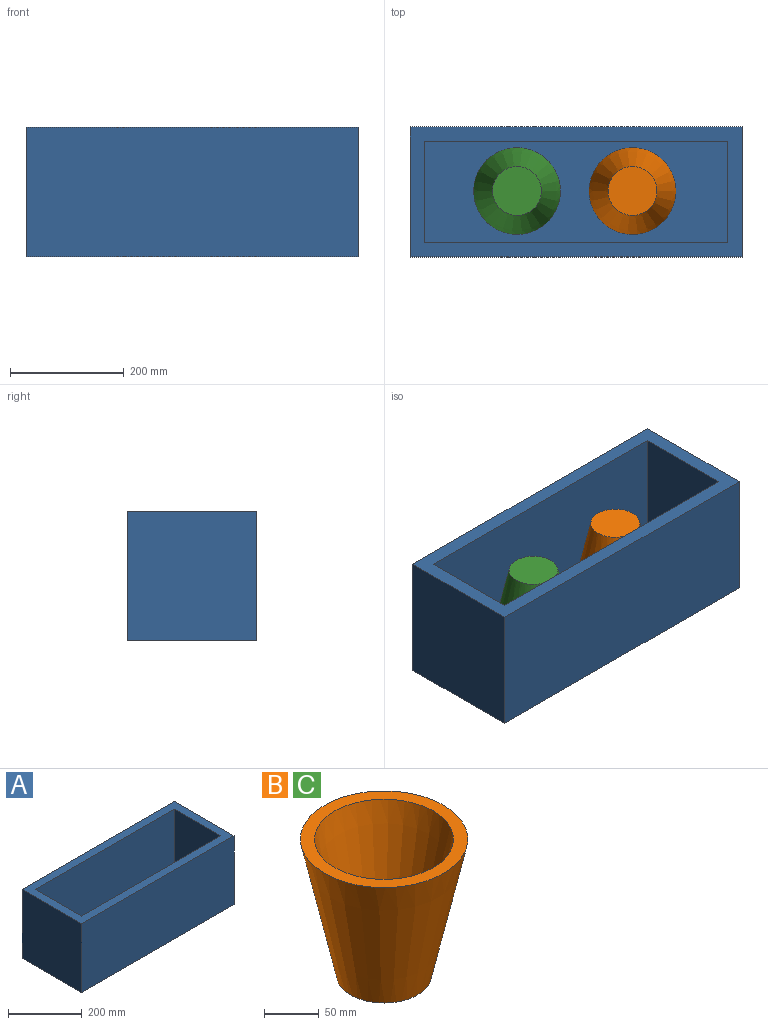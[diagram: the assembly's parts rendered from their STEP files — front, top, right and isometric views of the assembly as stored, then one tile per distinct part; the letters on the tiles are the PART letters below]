
ASSEMBLY  parts=3 mates=1
PART A: 11 faces, bbox 584.2x228.6x228.6 mm
  f0: plane 228.6x228.6mm, normal (-1,0,0), area 52258mm2, adj f1,f3,f4,f5
  f1: plane 584.2x228.6mm, normal (0,-1,0), area 133548.1mm2, adj f0,f2,f4,f5
  f2: plane 228.6x228.6mm, normal (1,0,0), area 52258mm2, adj f1,f3,f4,f5
  f3: plane 584.2x228.6mm, normal (0,1,0), area 133548.1mm2, adj f0,f2,f4,f5
  f4: plane 584.2x228.6mm, normal (0,0,1), area 38709.6mm2, adj f0,f1,f2,f3,f6,f7,f8,f9
  f5: plane 584.2x228.6mm, normal (0,0,-1), area 133548.1mm2, adj f0,f1,f2,f3
  f6: plane 203.2x177.8mm, normal (1,0,0), area 36129mm2, adj f4,f7,f9,f10
  f7: plane 533.4x203.2mm, normal (0,1,0), area 108386.9mm2, adj f4,f6,f8,f10
  f8: plane 203.2x177.8mm, normal (-1,0,0), area 36129mm2, adj f4,f7,f9,f10
  f9: plane 533.4x203.2mm, normal (0,-1,0), area 108386.9mm2, adj f4,f6,f8,f10
  f10: plane 533.4x177.8mm, normal (0,0,1), area 94838.5mm2, adj f6,f7,f8,f9
PART B: 5 faces, bbox 152.5x152.5x152.2 mm
  f0: cone r=76.24mm half-angle=89.8deg, axis (0,0,1), area 5701.5mm2, adj f1,f3
  f1: cone r=42.99mm half-angle=12.3deg, axis (0,0,1), area 58342.5mm2, adj f0,f2
  f2: plane 85.99x85.99mm, normal (0,0,-1), area 5807.2mm2, adj f1
  f3: cone r=30.59mm half-angle=12.3deg, axis (0,0,1), area 43035.1mm2, adj f0,f4
  f4: plane 65.54x65.54mm, normal (0,0,1), area 3373.6mm2, adj f3
PART C: same geometry as B
PLACE A t=(-414.86,-281.75,-319.09)mm fixed
PLACE B rot(axis=(1,0,0),180deg) t=(-309.89,-371.05,-217.34)mm
PLACE C rot(axis=(1,0,0),180deg) t=(-513.09,-371.05,-217.34)mm
MATE planar C.f0 <-> A.f10  axis (0,0,-1) through (-513.09,-371.05,-293.69)mm
